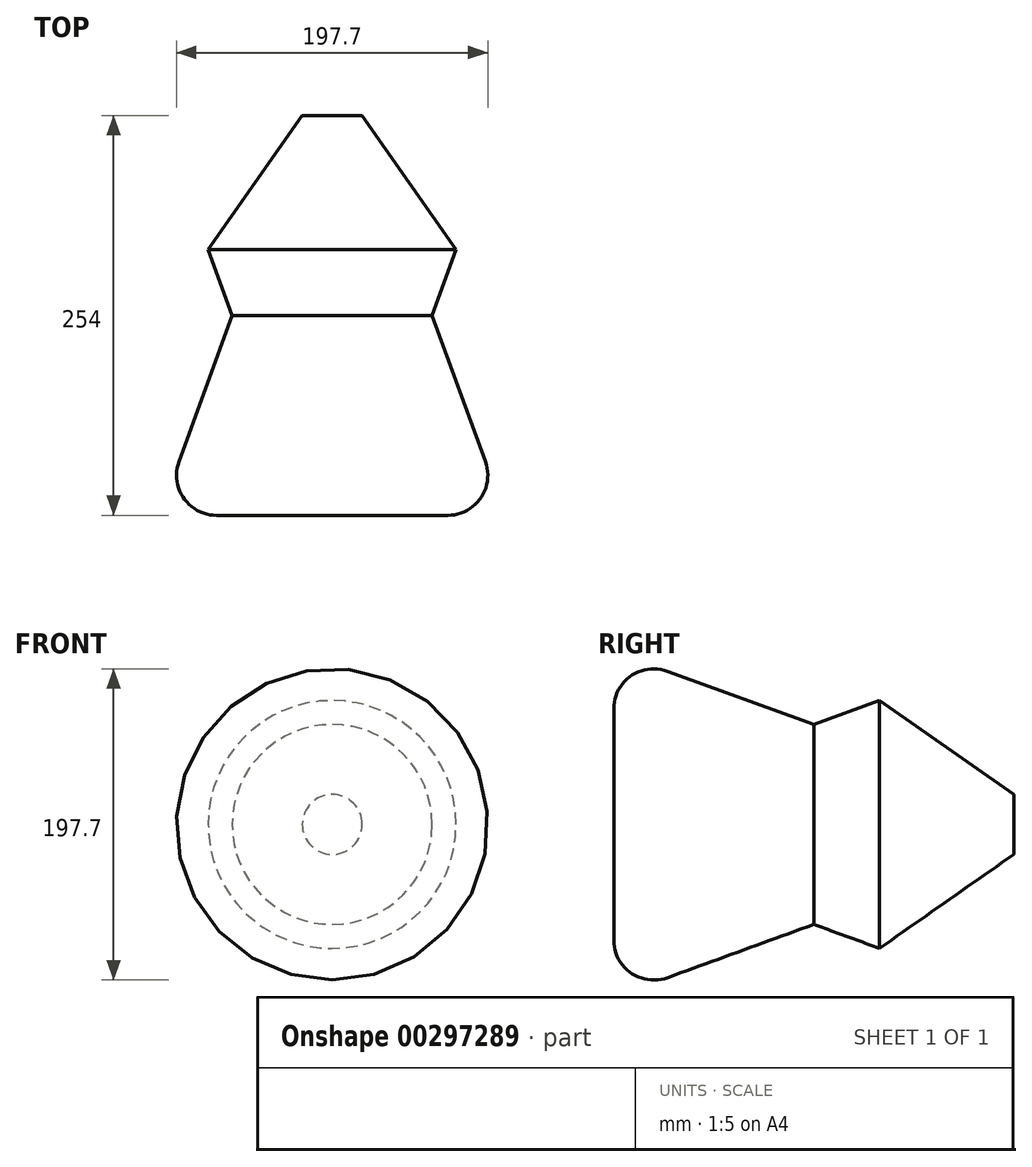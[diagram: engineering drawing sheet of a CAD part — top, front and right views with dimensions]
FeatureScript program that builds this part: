
annotation { "Feature Type Name" : "Feature", "Feature Type Description" : "" }
export const myFeature = defineFeature(function(context is Context, id is Id, definition is map)
    precondition{}
    {
        {
            var Q0;
            Q0=qCreatedBy(makeId("Front.planeOp"),FACE);
            var sketch = newSketch(context, id + "F0", { "sketchPlane" : qUnion([Q0])});
            skCircle(sketch, "E0", {"center": v(0, 0) * mm, "radius": 63.5 * mm});
            skSolve(sketch);
        }
        {
            var Q0;
            Q0 = qSketchRegion(id + "F0", true);
            extrude(context, id + "F1", {"entities" : qUnion([Q0]), "endBound" : BoundingType.SYMMETRIC, "depth" : 254 * mm, "hasDraft" : true, "draftAngle" : 20 * degree});
        }
        {
            var Q0;
            Q0=makeQuery(id+"F1.opExtrude","CAP_EDGE",EDGE,{"disambiguationData":[OSD([sQuery(id+"F0.wireOp",EDGE,"E0")])],"isStart":false});
            fillet(context, id + "F2", {"entities" : qUnion([Q0]), "radius" : 25.4 * mm, "tangentPropagation" : true, "allowEdgeOverflow" : false});
        }
        {
            var Q0;
            Q0=makeQuery(id+"F1.opExtrude","CAP_EDGE",EDGE,{"disambiguationData":[OSD([sQuery(id+"F0.wireOp",EDGE,"E0")])],"isStart":true});
            chamfer(context, id + "F3", {"entities" : qUnion([Q0]), "width" : 63.5 * mm, "tangentPropagation" : true});
        }
    });
